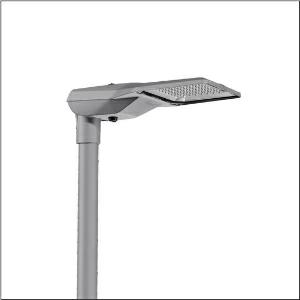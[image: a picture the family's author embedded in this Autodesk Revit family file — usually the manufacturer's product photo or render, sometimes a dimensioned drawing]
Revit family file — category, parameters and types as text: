
# Revit family: streetlight_sl_21_midi___pl52_5xe3h33t08lb_7b8b
name_source: partatom
category: Lighting Fixtures
units: mm (PartAtom-declared; Revit-internal decimal feet)

## family parameters
Cut with Voids When Loaded = No
Host = Face
Light Source = No
Part Type = Normal
Room Calculation Point = No
Round Connector Dimension = Use Diameter
Shared = No

## types (1)
- --- (1 x LED, 14100 lm, 98.3 W, 3000K)
    Apparent Load = 98 VA
    CIE Flux Codes = 27 59 98 100 100
    Color Rendering = 70
    Color Temperature = 3000K
    Default Elevation = 1800 mm
    Description = Streetlight SL 21 midi, mast luminaire, primary light control with lens, of PMMA, primary optical cover: cover, of toughened safety glass, transparent, light distribution: PL52, light emission: direct distribution, primary light characteristic: asymmetric, installation type: side-entry, post-top, LED, High Power LED, rated luminous flux: 14.100lm, luminous efficacy: 143lm/W, light colour: 730, colour temperature: 3000K, control: overheat protection, constant luminous flux control, time-dependent luminous flux control, flexible luminous flux parameterisation, presetting dimming logarithmic, mains connection: 230..240V, AC, 50/60Hz, start of lifetime: 98W, end of service life: 101W, reduction: 45W, luminaire housing, of diecast aluminium, powder-coated, Siteco® metallic grey (DB 702S), corrosivity category C5 mid according to DIN EN ISO 12944, please order mast flange separately, inclination adjustable: 0°, 5°, 10°, 15°, sealing non-destructively replaceable, multi-level sealing system, length: 644mm, width: 335mm, height: 110mm, mast flange for spigot size: 42mm (side-entry): 5XC10008XM4, 60/48mm (side-entry/post-top): 5XC10108XM2, 76/60mm (side-entry/post-top): 5XC10108XM1, Smart Interface below and above, protection rating (complete): IP66, insulation class (complete): insulation class II (safety insulation), certification: CE, ENEC, ENEC+, VDE, impact resistance: IK09, permissible operating ambient temperature for outdoor applications: -40..+50°C, standard-compliant lighting for roads and squares, packaging unit: 1 piece

Light Distribution: PL52
    Height = 111 mm
    Lamp = 1 x LED
    Lamp Light Flux = 14100 lm
    Lamp Power = 98.3 W
    Lamp count = 1
    Length = 644 mm
    Luminous efficacy = 143 lm/W
    Manufacturer = Siteco
    ModVariant = No
    Model = 5XE3H33T08LB
    Number of Poles = 1
    OnlyDefault = Yes
    Power Factor = 1
    Product Name = Streetlight SL 21 midi | PL52
    Product group = mast luminaire | pylon top
    ProductGroupID = 6100
    Protection Class = Protection class II
    Protection Degree = IP 66
    RLX_Detail_Level = 1
    RLX_Emergency_Light_Flux = 0 lm
    RLX_Emergency_Type = 0
    RLX_Emergency_Type_DB = No
    RlxData = <blob elided: 101381 chars, md5=0c6d3065>
    Socket = socket
    Standby Power = 0 W
    System Light Flux = 14100 lm
    System Power = 98 W
    Type Comments = factory setting: luminous flux: 100 % | dim-lin: 254 | 1020 mA
    Type Image = l_1004304.jpg
    URL = http://relux.com
    VarID = @adj_142989
    Voltage = 0 V
    Weight = 0.00 kg
    Width = 336 mm

## geometry (parser evidence)
native form markers: Blend x4, Sweep x11
no freeform markers — native parametric forms only
